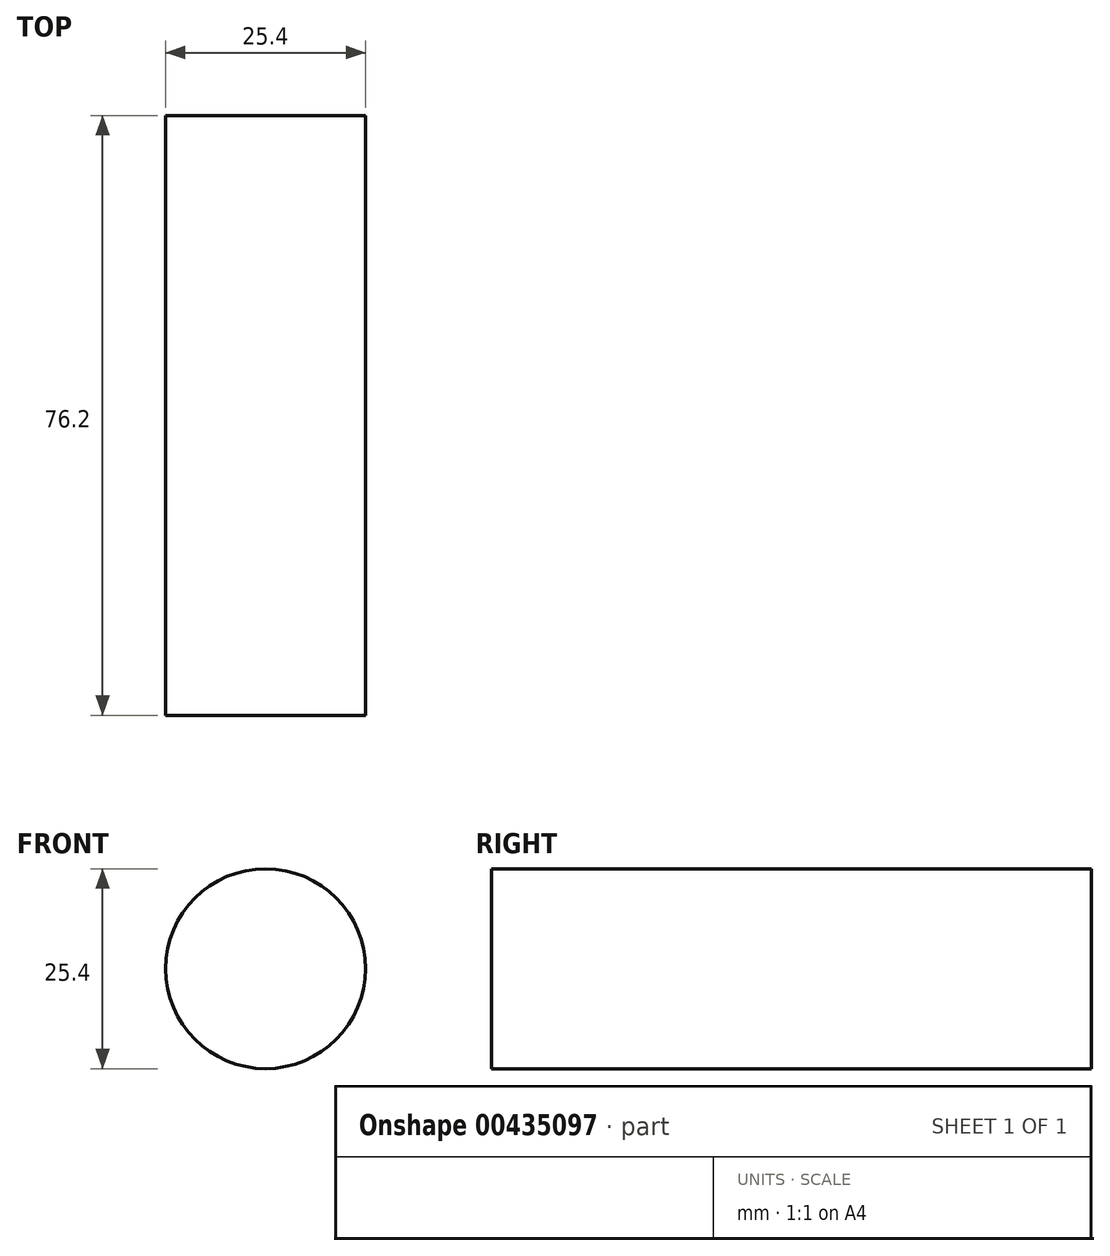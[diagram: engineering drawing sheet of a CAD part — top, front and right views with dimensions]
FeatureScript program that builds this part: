
annotation { "Feature Type Name" : "Feature", "Feature Type Description" : "" }
export const myFeature = defineFeature(function(context is Context, id is Id, definition is map)
    precondition{}
    {
        {
            var Q0;
            Q0=qCreatedBy(makeId("Front.planeOp"),FACE);
            var sketch = newSketch(context, id + "F0", { "sketchPlane" : qUnion([Q0])});
            skCircle(sketch, "E0", {"center": v(-28.45, 18.33) * mm, "radius": 12.7 * mm});
            skSolve(sketch);
        }
        {
            var Q0;
            Q0 = qSketchRegion(id + "F0", true);
            extrude(context, id + "F1", {"entities" : qUnion([Q0]), "depth" : 76.2 * mm});
        }
    });
